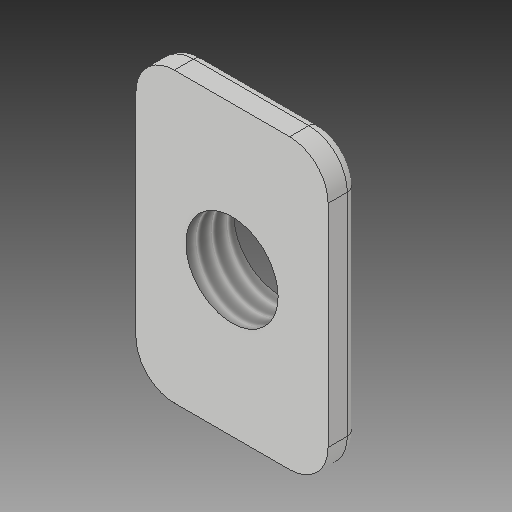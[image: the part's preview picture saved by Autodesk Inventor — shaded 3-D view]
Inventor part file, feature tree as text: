
AUTODESK INVENTOR PART (.ipt)
format: ipt  version: 2017 (Build 210142000, 142)  size: 143,872 bytes
history: native  units: mm
features: other x3, sketch x2
ambient origin geometry x8: Origin, YZ Plane, XZ Plane, XY Plane, X Axis, Y Axis, Z Axis, Center Point
bodies: Solid1 (feature_tree)
feature tree (5):
  other  "M5 Tee Nut.ipt"
  other  "Solid1::M5 Tee Nut.ipt"
  other  "TaggingFeature1"
  sketch  "Sketch1"  dims[d0=10.0mm]
  sketch  "Sketch2"
